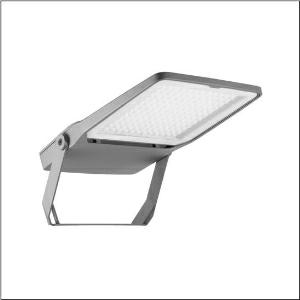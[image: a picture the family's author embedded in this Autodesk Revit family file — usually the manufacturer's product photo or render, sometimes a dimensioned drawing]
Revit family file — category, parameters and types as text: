
# Revit family: floodlight_fl_20_midi___pl61_5xa7681e2c1ac_9e02
name_source: partatom
category: Lighting Fixtures
units: mm (PartAtom-declared; Revit-internal decimal feet)

## family parameters
Cut with Voids When Loaded = No
Host = Face
Light Source = No
Part Type = Normal
Room Calculation Point = No
Round Connector Dimension = Use Diameter
Shared = No

## types (1)
- Floodlight FL 20 midi  PL61 (1 x LED 4000K / CRI = 70 (unbekannt), 27150 lm, 4000K)
    Apparent Load = 208 VA
    CIE Flux Codes = 33 65 98 100 100
    Color Rendering = 70
    Color Temperature = 4000K
    Default Elevation = 1800 mm
    Description = Floodlight FL 20 midi, floodlight, primary light control with lens, of plastic, primary optical cover: protective disc, of toughened safety glass, transparent, light distribution: PL61, light emission: direct distribution, primary light characteristic: asymmetric, installation type: surface-mounted, LED, High Power LED, rated luminous flux: 27.150lm, luminous efficacy: 131lm/W, light colour: 740, colour temperature: 4000K, control gear: ECG Basic, control: power reduction, overheat protection, electronic power reduction, with terminal, 5-pole, max. 2.5mm², mains connection: 220..240V, AC, 50/60Hz, rated input power: 208W, LED unit, of diecast aluminium, powder-coated, Siteco® metallic grey (DB 702S), corrosivity category C5 mid according to DIN EN ISO 12944, incl. 1x M20 cable gland for cable Ø 6.5..12mm, length: 654mm, width: 450mm, height: 76mm, housing frame, of diecast aluminium, powder-coated, Siteco® metallic grey (DB 702S), mounting bracket, of steel, powder-coated, Siteco® metallic grey (DB 702S), ON/OFF, protection rating (complete): IP66, insulation class (complete): insulation class I (protective earthing), certification: CE, ENEC, VDE, protection symbol: D, permissible operating ambient temperature: -40..+40°C, permissible operating ambient temperature for outdoor applications: -40..+50°C, standard: DIN EN 12944, packaging unit: 1 piece

Light Distribution: PL61
    Height = 76 mm
    Lamp = 1 x LED 4000K / CRI >= 70 (unbekannt)
    Lamp Light Flux = 27150 lm
    Lamp count = 1
    Length = 672 mm
    Luminous efficacy = 131 lm/W
    Manufacturer = Siteco
    ModVariant = No
    Model = 5XA7681E2C1AC
    Mounting Place = Wall
    Mounting Type = Surface mounted
    Number of Poles = 1
    OnlyDefault = Yes
    Power Factor = 1
    Product Name = Floodlight FL 20 midi | PL61
    Product group = floodlight | wall mounted
    ProductGroupID = 2001
    Protection Class = Protection class I
    Protection Degree = IP 66
    RLX_Detail_Level = 1
    RLX_Emergency_Light_Flux = 0 lm
    RLX_Emergency_Type = 0
    RLX_Emergency_Type_DB = No
    RlxData = <blob elided: 94289 chars, md5=f55be7dd>
    Socket = socket
    Standby Power = 0 W
    System Light Flux = 27150 lm
    System Power = 208 W
    Type Comments = Product without accessories
    Type Image = l_1005943.jpg
    URL = http://relux.com
    VarID = ---
    Voltage = 0 V
    Weight = 0.00 kg
    Width = 450 mm

## geometry (parser evidence)
native form markers: Blend x4, Sweep x13
no freeform markers — native parametric forms only
